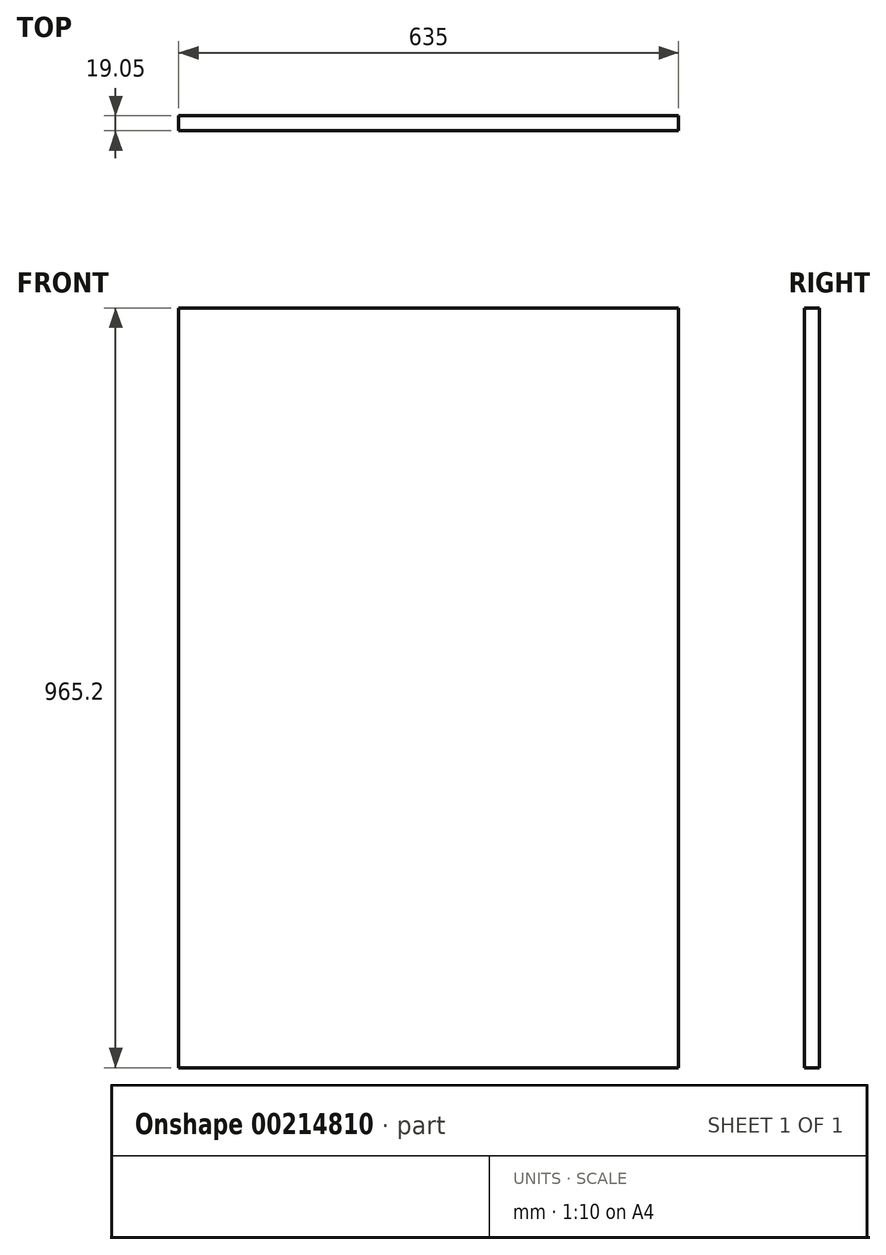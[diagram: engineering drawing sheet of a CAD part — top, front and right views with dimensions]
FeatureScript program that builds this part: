
annotation { "Feature Type Name" : "Feature", "Feature Type Description" : "" }
export const myFeature = defineFeature(function(context is Context, id is Id, definition is map)
    precondition{}
    {
        {
            var Q0;
            Q0=qCreatedBy(makeId("Front.planeOp"),FACE);
            var sketch = newSketch(context, id + "F0", { "sketchPlane" : qUnion([Q0])});
            skLineSegment(sketch, "E0.bottom", {"start": v(0, 0) * mm, "end": v(635, 0) * mm});
            skLineSegment(sketch, "E0.top", {"start": v(0, -965.2) * mm, "end": v(635, -965.2) * mm});
            skLineSegment(sketch, "E0.left", {"start": v(0, 0) * mm, "end": v(0, -965.2) * mm});
            skLineSegment(sketch, "E0.right", {"start": v(635, 0) * mm, "end": v(635, -965.2) * mm});
            skSolve(sketch);
        }
        {
            var Q0;
            Q0=makeQuery(id+"F0.imprint","IMPRINT",FACE,{"disambiguationData":[TD([[makeQuery(id+"F0.imprint","IMPRINT",EDGE,{"derivedFrom":sQuery(id+"F0.wireOp",EDGE,"E0.bottom")}),-1.0]])]});
            extrude(context, id + "F1", {"entities" : qUnion([Q0]), "depth" : 19.05 * mm});
        }
    });
